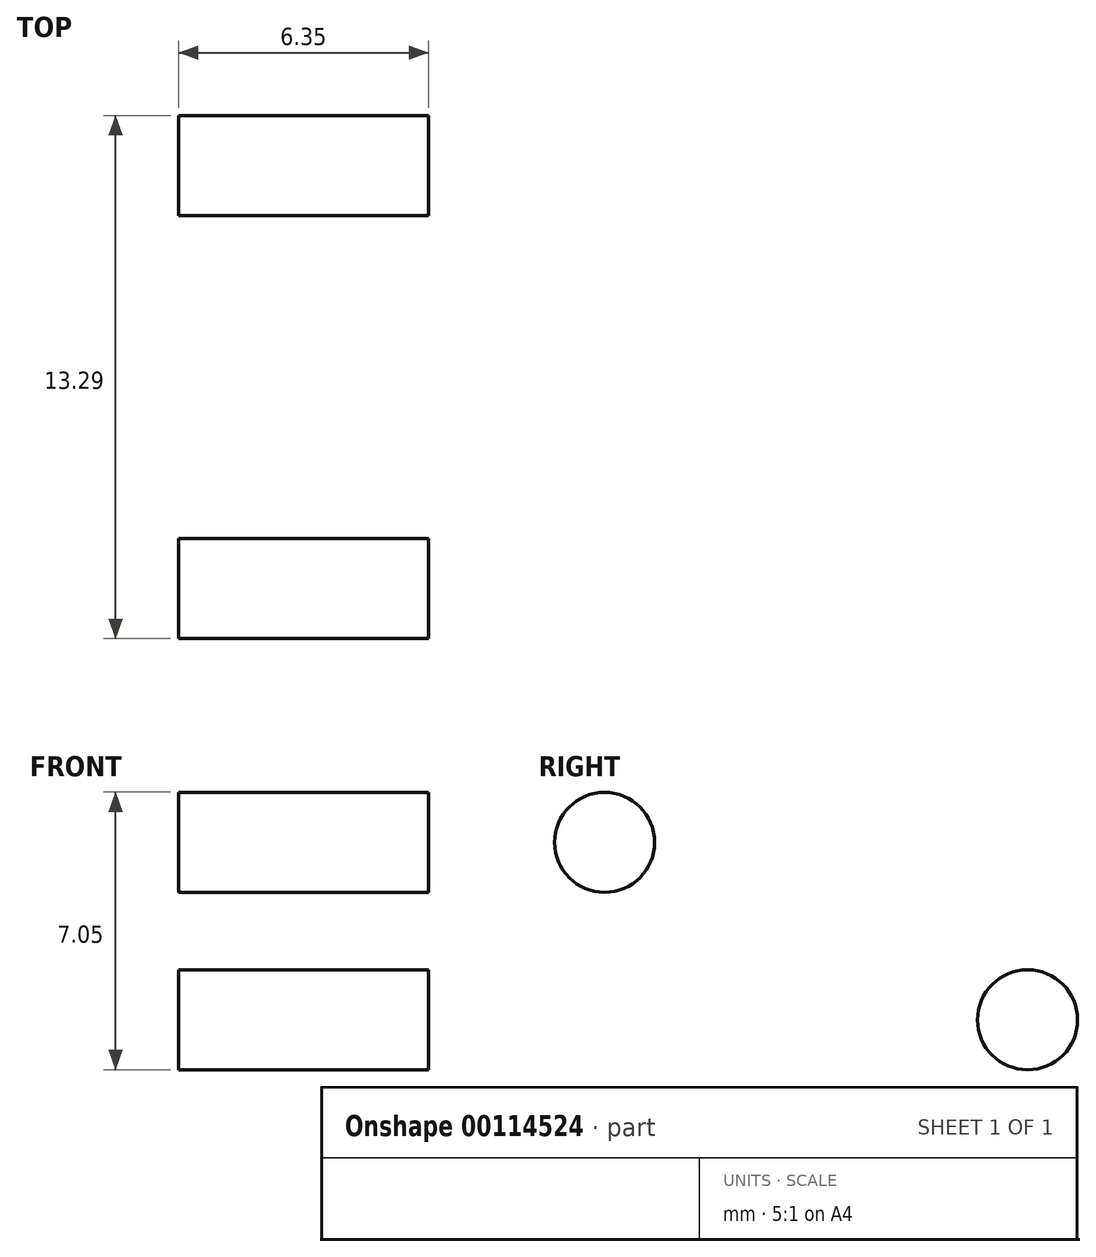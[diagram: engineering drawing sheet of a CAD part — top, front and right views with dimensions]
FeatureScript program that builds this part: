
annotation { "Feature Type Name" : "Feature", "Feature Type Description" : "" }
export const myFeature = defineFeature(function(context is Context, id is Id, definition is map)
    precondition{}
    {
        {
            var Q0;
            Q0=qCreatedBy(makeId("Right.planeOp"),FACE);
            var sketch = newSketch(context, id + "F0", { "sketchPlane" : qUnion([Q0])});
            skArc(sketch, "E0.0.startCap", {"start": v(120.44, -32.38) * mm, "mid": v(126.09, -43.05) * mm, "end": v(116.75, -50.7) * mm});
            skArc(sketch, "E0.0.endCap", {"start": v(-117.39, 46.76) * mm, "mid": v(-122.48, 59.23) * mm, "end": v(-110.02, 64.33) * mm});
            skLineSegment(sketch, "E0.0.left", {"start": v(40.36, -19.44) * mm, "end": v(-117.39, 46.76) * mm});
            skLineSegment(sketch, "E0.0.right", {"start": v(120.44, -32.38) * mm, "end": v(-93.74, 57.5) * mm});
            skArc(sketch, "E0.1.startCap", {"start": v(-92.8, -50.7) * mm, "mid": v(-102.32, -41.17) * mm, "end": v(-92.8, -31.64) * mm});
            skArc(sketch, "E0.1.endCap", {"start": v(120.44, -32.38) * mm, "mid": v(126.09, -43.05) * mm, "end": v(116.75, -50.7) * mm});
            skLineSegment(sketch, "E0.1.left", {"start": v(-92.8, -31.64) * mm, "end": v(37.9, -31.64) * mm});
            skLineSegment(sketch, "E0.1.right", {"start": v(-92.8, -50.7) * mm, "end": v(63.09, -50.7) * mm});
            skPoint(sketch, "E1", {"position": v(69.44, -31.64) * mm});
            skPoint(sketch, "E2", {"position": v(210.42, -39.26) * mm});
            skArc(sketch, "E3.filletArc", {"start": v(37.9, -31.64) * mm, "mid": v(44.12, -26.55) * mm, "end": v(40.36, -19.44) * mm});
            skArc(sketch, "E4.0.endCap", {"start": v(66.26, -31.64) * mm, "mid": v(69.44, -28.47) * mm, "end": v(72.61, -31.64) * mm});
            skLineSegment(sketch, "E4.0.left", {"start": v(66.26, -47.52) * mm, "end": v(66.26, -31.64) * mm});
            skLineSegment(sketch, "E4.0.right", {"start": v(72.61, -47.52) * mm, "end": v(72.61, -31.64) * mm});
            skLineSegment(sketch, "E5.trimOffspring", {"start": v(75.79, -50.7) * mm, "end": v(116.75, -50.7) * mm});
            skPoint(sketch, "E6.visualSharp", {"position": v(72.61, -50.7) * mm});
            skArc(sketch, "E6.filletArc", {"start": v(72.61, -47.52) * mm, "mid": v(73.54, -49.76) * mm, "end": v(75.79, -50.7) * mm});
            skPoint(sketch, "E7.visualSharp", {"position": v(66.26, -50.7) * mm});
            skArc(sketch, "E7.filletArc", {"start": v(63.09, -50.7) * mm, "mid": v(65.33, -49.76) * mm, "end": v(66.26, -47.52) * mm});
            skCircle(sketch, "E8", {"center": v(97.46, -32.38) * mm, "radius": 1.27 * mm});
            skCircle(sketch, "E9", {"center": v(108.2, -36.9) * mm, "radius": 1.27 * mm});
            skArc(sketch, "E10", {"start": v(-93.74, 57.5) * mm, "mid": v(-97.9, 55.8) * mm, "end": v(-99.6, 59.95) * mm});
            skLineSegment(sketch, "E11.trimOffspring", {"start": v(-99.6, 59.95) * mm, "end": v(-110.02, 64.33) * mm});
            skSolve(sketch);
        }
        {
            var Q0;
            Q0=makeQuery(id+"F0.imprint","IMPRINT",FACE,{"disambiguationData":[TD([[makeQuery(id+"F0.imprint","IMPRINT",EDGE,{"derivedFrom":sQuery(id+"F0.wireOp",EDGE,"E0.0.endCap")}),-1.0]])]});
            var Q1;
            Q1=makeQuery(id+"F0.imprint","IMPRINT",FACE,{"disambiguationData":[TD([[makeQuery(id+"F0.imprint","IMPRINT",EDGE,{"derivedFrom":sQuery(id+"F0.wireOp",EDGE,"E9")}),1.0]])]});
            var Q2;
            Q2=makeQuery(id+"F0.imprint","IMPRINT",FACE,{"disambiguationData":[TD([[makeQuery(id+"F0.imprint","IMPRINT",EDGE,{"derivedFrom":sQuery(id+"F0.wireOp",EDGE,"E8")}),1.0]])]});
            extrude(context, id + "F1", {"entities" : qUnion([Q0, Q1, Q2]), "depth" : 6.35 * mm});
        }
    });
